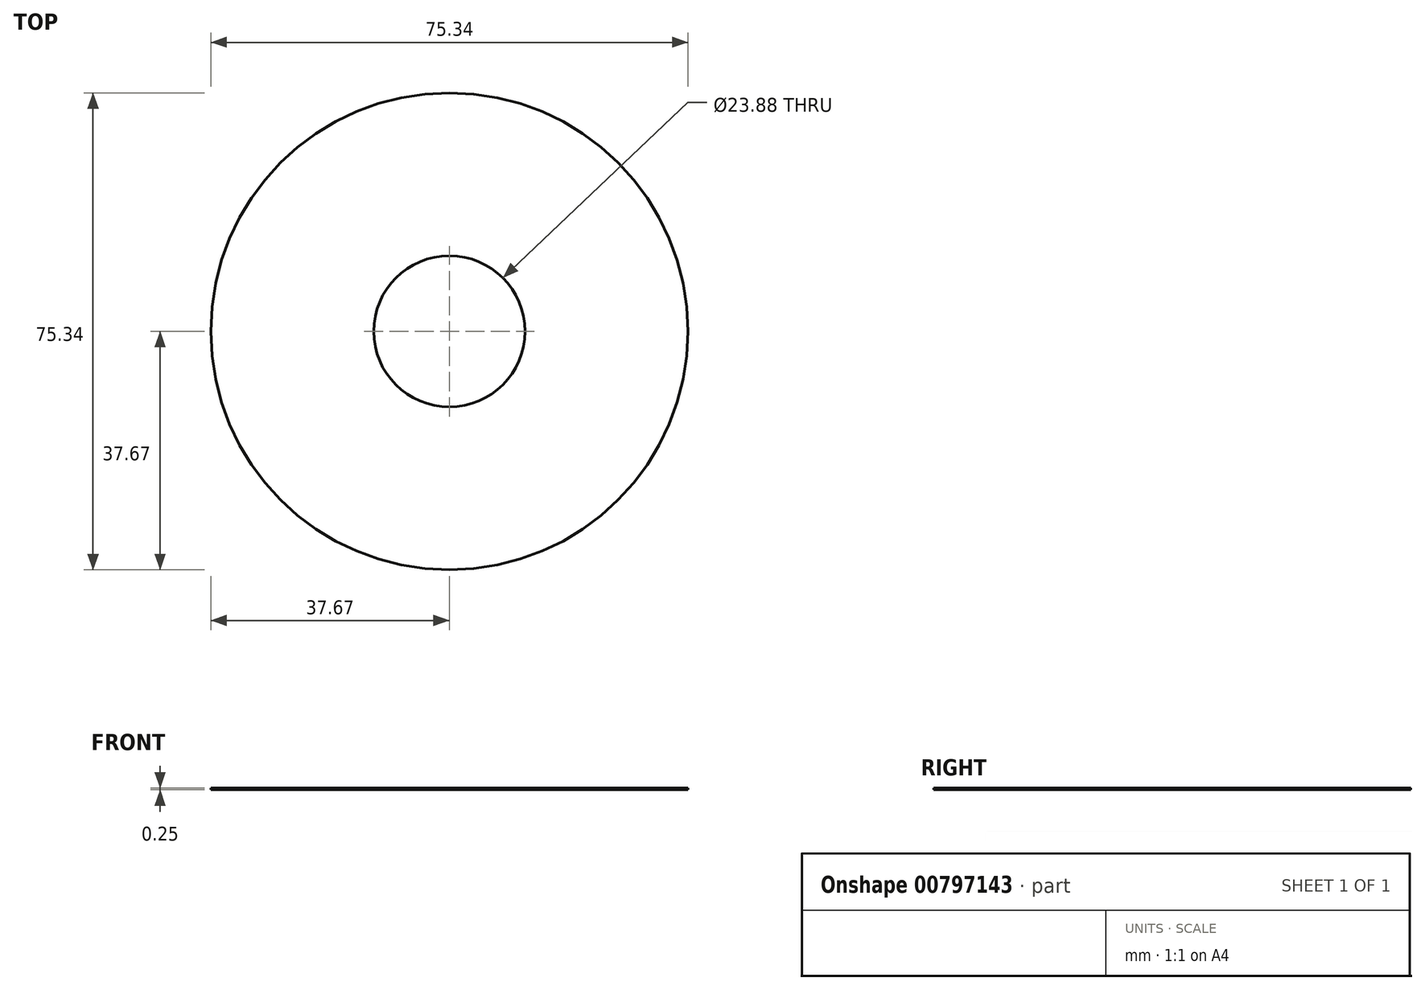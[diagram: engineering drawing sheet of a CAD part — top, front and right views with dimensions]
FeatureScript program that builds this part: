
annotation { "Feature Type Name" : "Feature", "Feature Type Description" : "" }
export const myFeature = defineFeature(function(context is Context, id is Id, definition is map)
    precondition{}
    {
        {
            var Q0;
            Q0=qCreatedBy(makeId("Top.planeOp"),FACE);
            var sketch = newSketch(context, id + "F0", { "sketchPlane" : qUnion([Q0])});
            skCircle(sketch, "E0", {"center": v(0, 0) * mm, "radius": 37.67 * mm});
            skCircle(sketch, "E1", {"center": v(0, 0) * mm, "radius": 11.94 * mm});
            skSolve(sketch);
        }
        {
            var Q0;
            Q0 = qSketchRegion(id + "F0", true);
            extrude(context, id + "F1", {"entities" : qUnion([Q0]), "depth" : 0.25 * mm, "offsetDistance" : 25.4 * mm});
        }
    });
